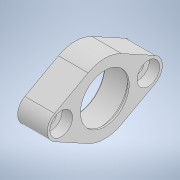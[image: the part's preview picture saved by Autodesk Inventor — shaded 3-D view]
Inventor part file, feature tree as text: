
AUTODESK INVENTOR PART (.ipt)
format: ipt  version: 2022 (Build 260153000, 153)  size: 163,840 bytes
history: native  units: in
note: dims shown in document units (in); Inventor stores cm internally (conversion verified against a paired STEP export)
features: other x3, extrude x2, sketch x2, chamfer x1, projected_geometry x1
ambient origin geometry x8: Origin, YZ Plane, XZ Plane, XY Plane, X Axis, Y Axis, Z Axis, Center Point
bodies: Solid1 (feature_tree)
feature tree (9):
  other  "XY Drive Bearing Holder.ipt"
  extrude  "Extrusion1"  Depth=0.1181in TaperAngle=0.0deg
  chamfer  "Chamfer1"  Distance=0.0197in Angle=45.0deg
  extrude  "Extrusion2"  [1 undecoded]
  other  "Solid3::XY Drive Bearing Holder.ipt"
  other  "TaggingFeature1"
  sketch  "Sketch1"  dims[d0=0.3937in d1=0.1181in d2=0.0in d3=0.0197in d4=0.125in d5=45.0deg]
  sketch  "Sketch2"  dims[d6=0.1181in d7=0.0in]
  projected_geometry  "Projected Loop1"
note: 1 required parameter value undecoded (feature->parameter linkage not recoverable at this tier; creation-order binding heuristic only, values carry confidence <= 0.55)
